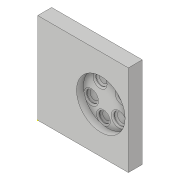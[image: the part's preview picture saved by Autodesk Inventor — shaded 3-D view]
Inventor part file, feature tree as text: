
AUTODESK INVENTOR PART (.ipt)
format: ipt  version: 2019 (Build 230136000, 136)  size: 218,624 bytes
history: native  units: in
note: dims shown in document units (in); Inventor stores cm internally (conversion verified against a paired STEP export)
features: thread x8, sketch x7, extrude x6, fillet x2
ambient origin geometry x8: Origin, YZ Plane, XZ Plane, XY Plane, X Axis, Y Axis, Z Axis, Center Point
bodies: Solid1 (feature_tree)
feature tree (23):
  extrude  "Extrusion1"  Depth=5.1181in
  extrude  "Extrusion2"  Depth=0.3937in
  thread  "Thread1"  [1 undecoded]
  thread  "Thread2"  [1 undecoded]
  thread  "Thread3"  [1 undecoded]
  thread  "Thread4"  [1 undecoded]
  thread  "Thread5"  [1 undecoded]
  thread  "Thread6"  [1 undecoded]
  thread  "Thread7"  [1 undecoded]
  thread  "Thread8"  [1 undecoded]
  extrude  "Extrusion3"  Depth=0.3937in
  fillet  "Fillet1"  Radius=0.3937in
  extrude  "Extrusion4"  Depth=0.3937in TaperAngle=0.0deg
  sketch  "Sketch5"  dims[d21=0.3937in d22=0.0in d23=0.3937in d24=0.0in]
  extrude  "Extrusion5"  Depth=0.3937in TaperAngle=0.0deg
  extrude  "Extrusion6"  Depth=0.3937in TaperAngle=0.0deg
  fillet  "Fillet2"  Radius=0.3937in
  sketch  "Sketch1"  dims[d0=5.1181in d1=5.1181in]
  sketch  "Sketch2"  dims[d2=0.7874in d3=0.0in d4=0.3937in d5=4.3307in d6=0.3937in d7=4.3307in d8=4.3307in d9=4.3307in d10=2.5591in d11=1.378in d12=0.3937in]
  sketch  "Sketch3"  dims[d13=0.3937in d14=0.3937in d15=0.3937in]
  sketch  "Sketch4"  dims[d17=0.0in d18=0.0in d19=0.3937in d20=0.0in]
  sketch  "Sketch6"  dims[d25=0.3937in d26=0.0in d27=0.3937in d28=0.0in d29=0.3937in d30=0.0in d31=0.3937in d32=0.0in]
  sketch  "Sketch7"  dims[d33=0.3937in d34=0.0in d37=0.3937in d38=2.3622in d39=2.3622in d40=0.7874in d41=0.2953in d42=0.0in d43=0.1969in d44=0.7874in d45=0.0in d46=0.3937in d47=0.0in d48=0.1969in d49=0.0in d50=0.0787in d51=1.1811in d52=0.4331in]
note: 8 required parameter values undecoded (feature->parameter linkage not recoverable at this tier; creation-order binding heuristic only, values carry confidence <= 0.55)
